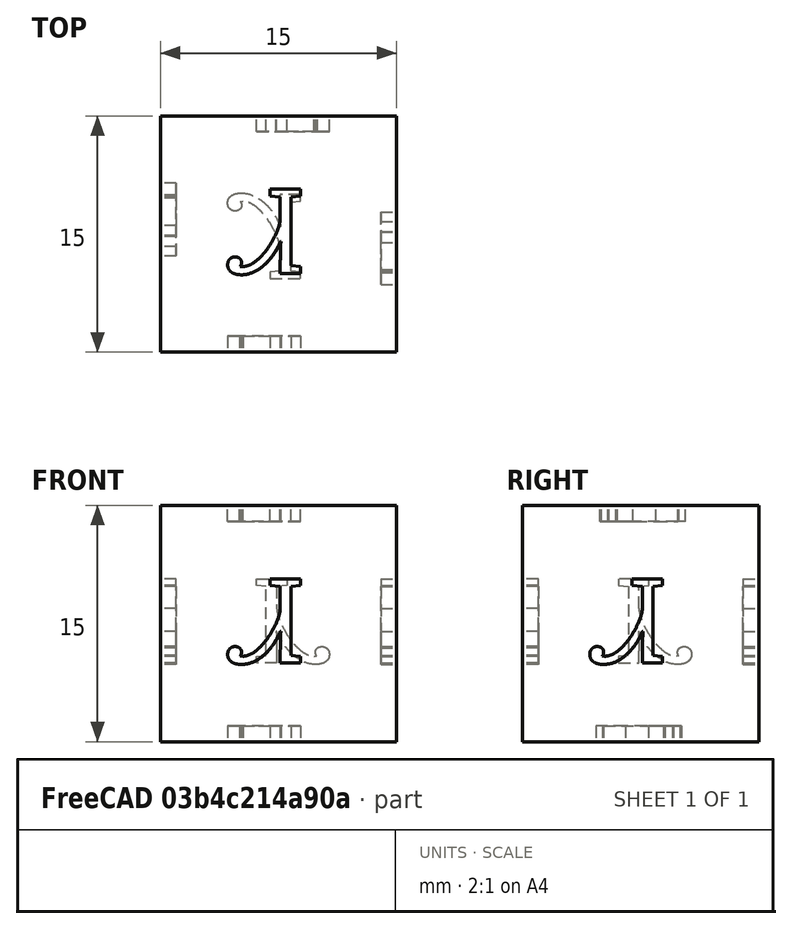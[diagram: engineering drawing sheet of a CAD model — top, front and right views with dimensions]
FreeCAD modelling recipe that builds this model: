
FCSTD DOCUMENT  (FreeCAD 0.18R16146 (Git))
Label: Ꮧ
License: All rights reserved
LicenseURL: http://en.wikipedia.org/wiki/All_rights_reserved
objects: Part::Part2DObjectPython×6, Part::Extrusion×6, Part::FeaturePython×6, Part::Box×1, PartDesign::Body×1
note: 20 computed .brp shape members not serialized (recipe doc carries the construction recipe); baked Part::Feature solids carry a one-line shape summary decoded from their .brp

FEATURE [Part::Box] Box  label="Cube"
  AttacherType = Attacher::AttachEngine3D
  Height = 15
  Length = 15
  Placement = pos=(-7.5,-7.5,-7.5) rot=(0,0,1;0rad)
  Width = 15
FEATURE [PartDesign::Body] Body
  Origin = -> Origin
FEATURE [Part::Part2DObjectPython] ShapeString  label="Face2"  # Draft 2D object (typed FeaturePython)
  AttachmentOffset = pos=(4,5,0) rot=(0,0,1;0rad)
  FontFile = <userpath>/Downloads/download/NotoSansCherokee-Regular.ttf
  MapMode = 5
  Placement = pos=(7.5,-3.5,-2.5) rot=(0.57735,0.57735,0.57735;2.0944rad)
  Size = 7.5
  String = Ꮧ
  Support = -> [Box]
  Tracking = 0
FEATURE [Part::Part2DObjectPython] ShapeString001  label="Face1"  # Draft 2D object (typed FeaturePython)
  AttachmentOffset = pos=(-11,5,0) rot=(0,0,1;0rad)
  FontFile = <userpath>/Downloads/download/NotoSansCherokee-Regular.ttf
  MapMode = 5
  Placement = pos=(-7.5,3.5,-2.5) rot=(0.57735,-0.57735,-0.57735;2.0944rad)
  Size = 7.5
  String = Ꮧ
  Support = -> [Box]
  Tracking = 0
FEATURE [Part::Part2DObjectPython] ShapeString003  label="Face4"  # Draft 2D object (typed FeaturePython)
  AttachmentOffset = pos=(-11,5,0) rot=(0,0,1;0rad)
  FontFile = <userpath>/Downloads/download/NotoSansCherokee-Regular.ttf
  MapMode = 5
  Placement = pos=(3.5,7.5,-2.5) rot=(0,0.707107,0.707107;3.14159rad)
  Size = 7.5
  String = Ꮧ
  Support = -> [Box]
  Tracking = 0
FEATURE [Part::Part2DObjectPython] ShapeString004  label="Face3"  # Draft 2D object (typed FeaturePython)
  AttachmentOffset = pos=(4,5,0) rot=(0,0,1;0rad)
  FontFile = <userpath>/Downloads/download/NotoSansCherokee-Regular.ttf
  MapMode = 5
  Placement = pos=(-3.5,-7.5,-2.5) rot=(1,0,0;1.5708rad)
  Size = 7.5
  String = Ꮧ
  Support = -> [Box]
  Tracking = 0
FEATURE [Part::Part2DObjectPython] ShapeString005  label="Face6"  # Draft 2D object (typed FeaturePython)
  AttachmentOffset = pos=(4,5,0) rot=(0,0,1;0rad)
  FontFile = <userpath>/Downloads/download/NotoSansCherokee-Regular.ttf
  MapMode = 5
  Placement = pos=(-3.5,-2.5,7.5) rot=(0,0,1;0rad)
  Size = 7.5
  String = Ꮧ
  Support = -> [Box]
  Tracking = 0
FEATURE [Part::Part2DObjectPython] ShapeString006  label="Face5"  # Draft 2D object (typed FeaturePython)
  AttachmentOffset = pos=(4,-10,0) rot=(0,0,1;0rad)
  FontFile = <userpath>/Downloads/download/NotoSansCherokee-Regular.ttf
  MapMode = 5
  Placement = pos=(-3.5,2.5,-7.5) rot=(1,0,0;3.14159rad)
  Size = 7.5
  String = Ꮧ
  Support = -> [Box]
  Tracking = 0
FEATURE [Part::Extrusion] Extrude
  Base = -> ShapeString
  Dir = (1,0,0)
  DirMode = 2
  FaceMakerClass = Part::FaceMakerBullseye
  LengthFwd = 1
  LengthRev = 1
  Solid = false
  Symmetric = false
FEATURE [Part::Extrusion] Extrude001
  Base = -> ShapeString001
  Dir = (-1,0,0)
  DirMode = 2
  FaceMakerClass = Part::FaceMakerBullseye
  LengthFwd = 1
  LengthRev = 1
  Solid = false
  Symmetric = false
FEATURE [Part::Extrusion] Extrude002
  Base = -> ShapeString003
  Dir = (0,1,-2e-16)
  DirMode = 2
  FaceMakerClass = Part::FaceMakerBullseye
  LengthFwd = 1
  LengthRev = 1
  Solid = false
  Symmetric = false
FEATURE [Part::Extrusion] Extrude003
  Base = -> ShapeString004
  Dir = (0,-1,2e-16)
  DirMode = 2
  FaceMakerClass = Part::FaceMakerBullseye
  LengthFwd = 1
  LengthRev = 1
  Solid = false
  Symmetric = false
FEATURE [Part::Extrusion] Extrude004
  Base = -> ShapeString006
  Dir = (0,0,-1)
  DirMode = 2
  FaceMakerClass = Part::FaceMakerBullseye
  LengthFwd = 1
  LengthRev = 1
  Solid = false
  Symmetric = false
FEATURE [Part::Extrusion] Extrude005
  Base = -> ShapeString005
  Dir = (0,0,1)
  DirMode = 2
  FaceMakerClass = Part::FaceMakerBullseye
  LengthFwd = 1
  LengthRev = 1
  Solid = false
  Symmetric = false
FEATURE [Part::FeaturePython] Cutout  # WARN: FeaturePython — macro-defined, semantics opaque (R4)
  Base = -> Box
  Tolerance = 0
  Tool = -> Extrude003
FEATURE [Part::FeaturePython] Cutout001  # WARN: FeaturePython — macro-defined, semantics opaque (R4)
  Base = -> Cutout
  Tolerance = 0
  Tool = -> Extrude005
FEATURE [Part::FeaturePython] Cutout002  # WARN: FeaturePython — macro-defined, semantics opaque (R4)
  Base = -> Cutout001
  Tolerance = 0
  Tool = -> Extrude004
FEATURE [Part::FeaturePython] Cutout003  # WARN: FeaturePython — macro-defined, semantics opaque (R4)
  Base = -> Cutout002
  Tolerance = 0
  Tool = -> Extrude
FEATURE [Part::FeaturePython] Cutout004  # WARN: FeaturePython — macro-defined, semantics opaque (R4)
  Base = -> Cutout003
  Tolerance = 0
  Tool = -> Extrude001
FEATURE [Part::FeaturePython] Cutout005  # WARN: FeaturePython — macro-defined, semantics opaque (R4)
  Base = -> Cutout004
  Tolerance = 0
  Tool = -> Extrude002
